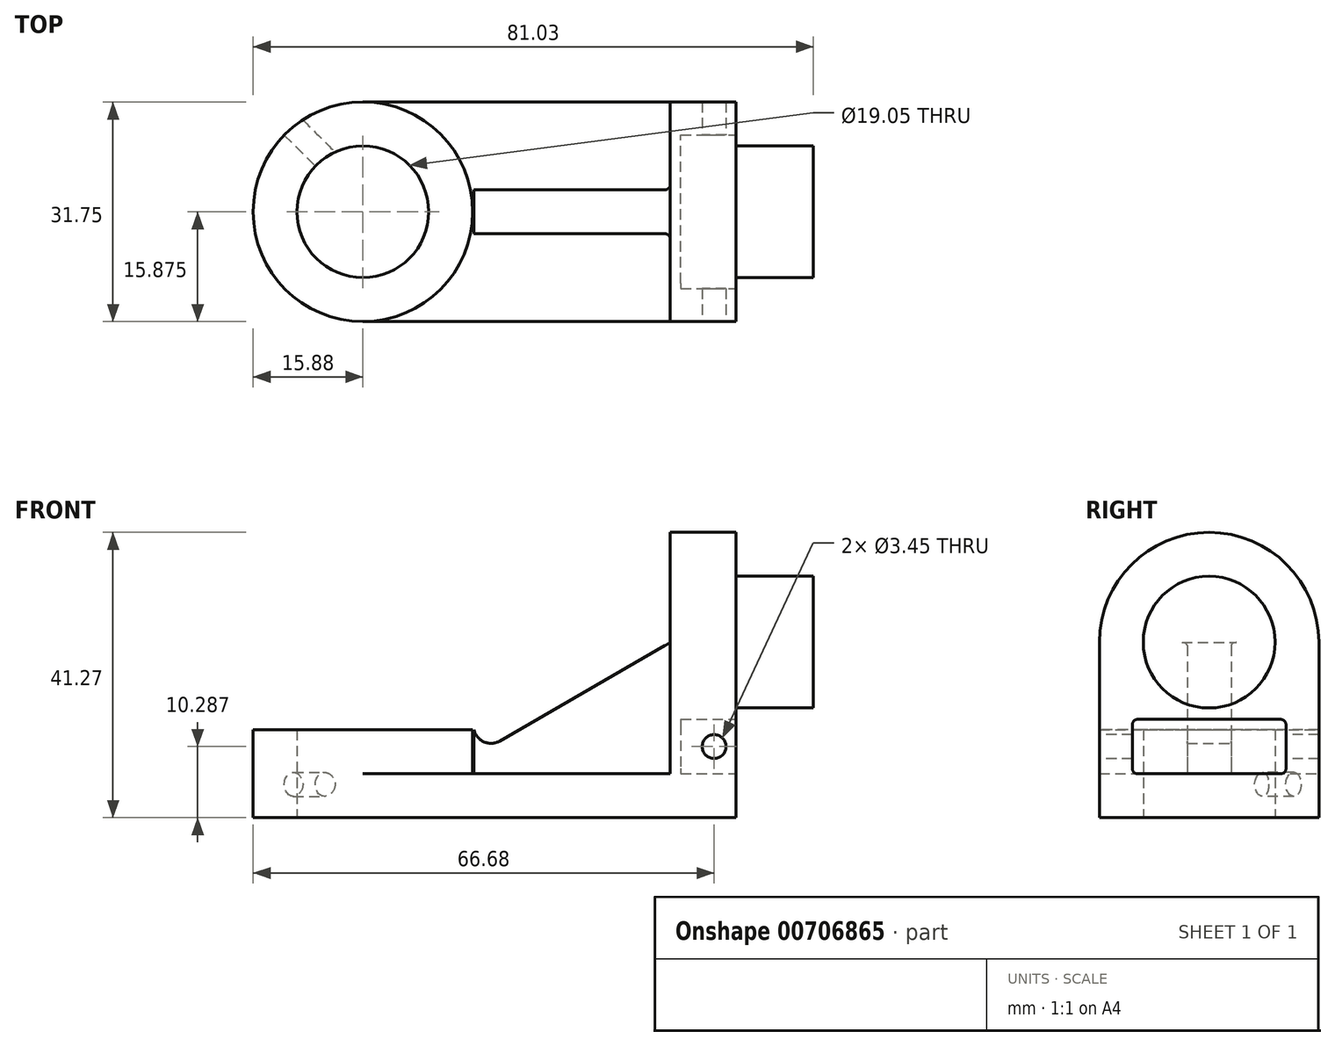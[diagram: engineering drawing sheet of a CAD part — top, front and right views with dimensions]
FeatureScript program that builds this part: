
annotation { "Feature Type Name" : "Feature", "Feature Type Description" : "" }
export const myFeature = defineFeature(function(context is Context, id is Id, definition is map)
    precondition{}
    {
        {
            var Q0;
            Q0=qCreatedBy(makeId("Front.planeOp"),FACE);
            var sketch = newSketch(context, id + "F0", { "sketchPlane" : qUnion([Q0])});
            skLineSegment(sketch, "E0", {"start": v(0, 0) * mm, "end": v(53.97, 0) * mm});
            skLineSegment(sketch, "E1", {"start": v(53.97, 0) * mm, "end": v(53.97, 6.35) * mm});
            skLineSegment(sketch, "E2", {"start": v(53.98, 6.35) * mm, "end": v(0, 6.35) * mm});
            skLineSegment(sketch, "E3", {"start": v(0, 6.35) * mm, "end": v(0, 0) * mm});
            skSolve(sketch);
        }
        {
            var Q0;
            Q0 = qSketchRegion(id + "F0", true);
            extrude(context, id + "F1", {"entities" : qUnion([Q0]), "oppositeDirection" : true, "depth" : 31.75 * mm, "offsetDistance" : 25.4 * mm});
        }
        {
            var Q0;
            Q0=makeQuery(id+"F1.opExtrude","SWEPT_FACE",FACE,{"disambiguationData":[OSD([sQuery(id+"F0.wireOp",EDGE,"E1")])]});
            var sketch = newSketch(context, id + "F2", { "sketchPlane" : qUnion([Q0])});
            skLineSegment(sketch, "E4", {"start": v(0, 0) * mm, "end": v(0, 25.4) * mm});
            skLineSegment(sketch, "E5", {"start": v(0, 0) * mm, "end": v(31.75, 0) * mm});
            skLineSegment(sketch, "E6", {"start": v(31.75, 0) * mm, "end": v(31.75, 25.4) * mm});
            skArc(sketch, "E7", {"start": v(31.75, 25.4) * mm, "mid": v(15.88, 41.28) * mm, "end": v(0, 25.4) * mm});
            skSolve(sketch);
        }
        {
            var Q0;
            Q0 = qSketchRegion(id + "F2", true);
            extrude(context, id + "F3", {"entities" : qUnion([Q0]), "operationType" : NewBodyOperationType.ADD, "oppositeDirection" : true, "depth" : 9.52 * mm, "offsetDistance" : 25.4 * mm});
        }
        {
            var Q0;
            Q0=makeQuery(id+"F3.boolean.opBoolean","MERGE",FACE,{"derivedFrom":[makeQuery(id+"F1.opExtrude","SWEPT_FACE",FACE,{"disambiguationData":[OSD([sQuery(id+"F0.wireOp",EDGE,"E1")])]}),makeQuery(id+"F3.opExtrude","CAP_FACE",FACE,{"disambiguationData":[OSD([sQuery(id+"F2.wireOp",EDGE,"E4"),sQuery(id+"F2.wireOp",EDGE,"E5"),sQuery(id+"F2.wireOp",EDGE,"E6"),sQuery(id+"F2.wireOp",EDGE,"E7")])],"isStart":true})]});
            var sketch = newSketch(context, id + "F4", { "sketchPlane" : qUnion([Q0])});
            skCircle(sketch, "E8", {"center": v(15.88, 25.4) * mm, "radius": 9.53 * mm});
            skSolve(sketch);
        }
        {
            var Q0;
            Q0 = qSketchRegion(id + "F4", true);
            extrude(context, id + "F5", {"entities" : qUnion([Q0]), "operationType" : NewBodyOperationType.ADD, "depth" : 11.18 * mm, "offsetDistance" : 25.4 * mm});
        }
        {
            var Q0;
            Q0=makeQuery(id+"F1.opExtrude","SWEPT_FACE",FACE,{"disambiguationData":[OSD([sQuery(id+"F0.wireOp",EDGE,"E0")])]});
            var sketch = newSketch(context, id + "F6", { "sketchPlane" : qUnion([Q0])});
            skCircle(sketch, "E9", {"center": v(0, -15.88) * mm, "radius": 15.88 * mm});
            skCircle(sketch, "E10", {"center": v(0, -15.88) * mm, "radius": 9.53 * mm});
            skSolve(sketch);
        }
        {
            var Q0;
            Q0 = qSketchRegion(id + "F6", true);
            extrude(context, id + "F7", {"entities" : qUnion([Q0]), "operationType" : NewBodyOperationType.ADD, "oppositeDirection" : true, "depth" : 12.7 * mm, "offsetDistance" : 25.4 * mm});
        }
        {
            var Q0;
            Q0=makeQuery(id+"F7.boolean.opBoolean","SPLIT",FACE,{"disambiguationData":[TD([makeQuery(id+"F1.opExtrude","SWEPT_FACE",FACE,{"disambiguationData":[OSD([sQuery(id+"F0.wireOp",EDGE,"E3")])]})])],"derivedFrom":makeQuery(id+"F1.opExtrude","SWEPT_FACE",FACE,{"disambiguationData":[OSD([sQuery(id+"F0.wireOp",EDGE,"E2")])]})});
            extrude(context, id + "F8", {"entities" : qUnion([Q0]), "operationType" : NewBodyOperationType.REMOVE, "oppositeDirection" : true, "depth" : 25.4 * mm, "offsetDistance" : 25.4 * mm});
        }
        {
            var Q0;
            Q0=makeQuery(id+"F3.boolean.opBoolean","MERGE",FACE,{"derivedFrom":[makeQuery(id+"F1.opExtrude","SWEPT_FACE",FACE,{"disambiguationData":[OSD([sQuery(id+"F0.wireOp",EDGE,"E1")])]}),makeQuery(id+"F3.opExtrude","CAP_FACE",FACE,{"disambiguationData":[OSD([sQuery(id+"F2.wireOp",EDGE,"E4"),sQuery(id+"F2.wireOp",EDGE,"E5"),sQuery(id+"F2.wireOp",EDGE,"E6"),sQuery(id+"F2.wireOp",EDGE,"E7")])],"isStart":true})]});
            var sketch = newSketch(context, id + "F9", { "sketchPlane" : qUnion([Q0])});
            skLineSegment(sketch, "E11.bottom", {"start": v(4.78, 14.22) * mm, "end": v(27, 14.22) * mm});
            skLineSegment(sketch, "E11.top", {"start": v(4.78, 6.35) * mm, "end": v(27, 6.35) * mm});
            skLineSegment(sketch, "E11.left", {"start": v(4.78, 14.22) * mm, "end": v(4.78, 6.35) * mm});
            skLineSegment(sketch, "E11.right", {"start": v(27, 14.22) * mm, "end": v(27, 6.35) * mm});
            skSolve(sketch);
        }
        {
            var Q0;
            Q0 = qSketchRegion(id + "F9", true);
            extrude(context, id + "F10", {"entities" : qUnion([Q0]), "operationType" : NewBodyOperationType.REMOVE, "oppositeDirection" : true, "depth" : 8 * mm, "offsetDistance" : 25.4 * mm});
        }
        {
            var Q0;
            Q0=makeQuery(id+"F3.boolean.opBoolean","MERGE",FACE,{"derivedFrom":[makeQuery(id+"F1.opExtrude","CAP_FACE",FACE,{"disambiguationData":[OSD([sQuery(id+"F0.wireOp",EDGE,"E0"),sQuery(id+"F0.wireOp",EDGE,"E1"),sQuery(id+"F0.wireOp",EDGE,"E2"),sQuery(id+"F0.wireOp",EDGE,"E3")])],"isStart":true}),makeQuery(id+"F3.opExtrude","SWEPT_FACE",FACE,{"disambiguationData":[OSD([sQuery(id+"F2.wireOp",EDGE,"E4")])]})]});
            var sketch = newSketch(context, id + "F11", { "sketchPlane" : qUnion([Q0])});
            skCircle(sketch, "E12", {"center": v(50.8, 10.29) * mm, "radius": 1.73 * mm});
            skSolve(sketch);
        }
        {
            var Q0;
            Q0 = qSketchRegion(id + "F11", true);
            extrude(context, id + "F12", {"entities" : qUnion([Q0]), "operationType" : NewBodyOperationType.REMOVE, "oppositeDirection" : true, "depth" : 31.75 * mm, "offsetDistance" : 25.4 * mm});
        }
        {
            var Q0;
            Q0=makeQuery(id+"F10.boolean.opBoolean","COPY",EDGE,{"derivedFrom":makeQuery(id+"F10.opExtrude","SWEPT_EDGE",EDGE,{"disambiguationData":[OSD([sQuery(id+"F9.wireOp",EDGE,"E11.top"),sQuery(id+"F9.wireOp",EDGE,"E11.right")])]})});
            var Q1;
            Q1=makeQuery(id+"F10.boolean.opBoolean","COPY",EDGE,{"derivedFrom":makeQuery(id+"F10.opExtrude","SWEPT_EDGE",EDGE,{"disambiguationData":[OSD([sQuery(id+"F9.wireOp",EDGE,"E11.bottom"),sQuery(id+"F9.wireOp",EDGE,"E11.right")])]})});
            var Q2;
            Q2=makeQuery(id+"F10.boolean.opBoolean","COPY",EDGE,{"derivedFrom":makeQuery(id+"F10.opExtrude","SWEPT_EDGE",EDGE,{"disambiguationData":[OSD([sQuery(id+"F9.wireOp",EDGE,"E11.top"),sQuery(id+"F9.wireOp",EDGE,"E11.left")])]})});
            var Q3;
            Q3=makeQuery(id+"F10.boolean.opBoolean","COPY",EDGE,{"derivedFrom":makeQuery(id+"F10.opExtrude","SWEPT_EDGE",EDGE,{"disambiguationData":[OSD([sQuery(id+"F9.wireOp",EDGE,"E11.bottom"),sQuery(id+"F9.wireOp",EDGE,"E11.left")])]})});
            fillet(context, id + "F13", {"entities" : qUnion([Q0, Q1, Q2, Q3]), "radius" : 0.76 * mm, "tangentPropagation" : true, "allowEdgeOverflow" : false});
        }
        {
            var Q0;
            Q0=qCreatedBy(makeId("Front.planeOp"),FACE);
            cPlane(context, id + "F14", {"entities" : qUnion([Q0]), "cplaneType" : CPlaneType.OFFSET, "offset" : 15.88 * mm, "oppositeDirection" : true, "width" : 152.4 * mm, "height" : 152.4 * mm});
        }
        {
            var Q0;
            Q0=qCreatedBy(id+"F14.planeOp",FACE);
            var Q1;
            Q1=qCreatedBy(makeId("Right.planeOp"),FACE);
            cPlane(context, id + "F15", {"entities" : qUnion([Q0, Q1]), "cplaneType" : CPlaneType.MID_PLANE, "offset" : 25.4 * mm, "flipAlignment" : true, "width" : 152.4 * mm, "height" : 152.4 * mm});
        }
        {
            var Q0;
            Q0=qCreatedBy(id+"F14.planeOp",FACE);
            var sketch = newSketch(context, id + "F16", { "sketchPlane" : qUnion([Q0])});
            skLineSegment(sketch, "E13", {"start": v(16.07, 12.7) * mm, "end": v(16.07, 6.35) * mm});
            skLineSegment(sketch, "E14", {"start": v(16.07, 6.35) * mm, "end": v(44.57, 6.35) * mm});
            skLineSegment(sketch, "E15", {"start": v(44.57, 6.35) * mm, "end": v(44.57, 25.4) * mm});
            skLineSegment(sketch, "E16", {"start": v(44.57, 25.4) * mm, "end": v(19.8, 11.1) * mm});
            skArc(sketch, "E17", {"start": v(16.07, 12.7) * mm, "mid": v(17.54, 10.97) * mm, "end": v(19.8, 11.1) * mm});
            skSolve(sketch);
        }
        {
            var Q0;
            Q0 = qSketchRegion(id + "F16", true);
            extrude(context, id + "F17", {"entities" : qUnion([Q0]), "operationType" : NewBodyOperationType.ADD, "endBound" : BoundingType.SYMMETRIC, "depth" : 6.35 * mm, "offsetDistance" : 25.4 * mm});
        }
        {
            var Q0;
            Q0=makeQuery(id+"F17.boolean.opBoolean","INTERSECT",EDGE,{"derivedFrom":[makeQuery(id+"F3.opExtrude","CAP_FACE",FACE,{"disambiguationData":[OSD([sQuery(id+"F2.wireOp",EDGE,"E4"),sQuery(id+"F2.wireOp",EDGE,"E5"),sQuery(id+"F2.wireOp",EDGE,"E6"),sQuery(id+"F2.wireOp",EDGE,"E7")])],"isStart":false}),makeQuery(id+"F17.opExtrude","CAP_FACE",FACE,{"disambiguationData":[OSD([sQuery(id+"F16.wireOp",EDGE,"E13"),sQuery(id+"F16.wireOp",EDGE,"E14"),sQuery(id+"F16.wireOp",EDGE,"E15"),sQuery(id+"F16.wireOp",EDGE,"E16"),sQuery(id+"F16.wireOp",EDGE,"E17")])],"isStart":false})]});
            var Q1;
            Q1=makeQuery(id+"F17.boolean.opBoolean","INTERSECT",EDGE,{"derivedFrom":[makeQuery(id+"F3.opExtrude","CAP_FACE",FACE,{"disambiguationData":[OSD([sQuery(id+"F2.wireOp",EDGE,"E4"),sQuery(id+"F2.wireOp",EDGE,"E5"),sQuery(id+"F2.wireOp",EDGE,"E6"),sQuery(id+"F2.wireOp",EDGE,"E7")])],"isStart":false}),makeQuery(id+"F17.opExtrude","CAP_FACE",FACE,{"disambiguationData":[OSD([sQuery(id+"F16.wireOp",EDGE,"E13"),sQuery(id+"F16.wireOp",EDGE,"E14"),sQuery(id+"F16.wireOp",EDGE,"E15"),sQuery(id+"F16.wireOp",EDGE,"E16"),sQuery(id+"F16.wireOp",EDGE,"E17")])],"isStart":true})]});
            fillet(context, id + "F18", {"entities" : qUnion([Q0, Q1]), "radius" : 0.76 * mm, "tangentPropagation" : true, "allowEdgeOverflow" : false});
        }
        {
            var Q0;
            Q0=qCreatedBy(id+"F15.planeOp",FACE);
            var sketch = newSketch(context, id + "F19", { "sketchPlane" : qUnion([Q0])});
            skCircle(sketch, "E18", {"center": v(12.76, 4.83) * mm, "radius": 1.73 * mm});
            skSolve(sketch);
        }
        {
            var Q0;
            Q0 = qSketchRegion(id + "F19", true);
            extrude(context, id + "F20", {"entities" : qUnion([Q0]), "operationType" : NewBodyOperationType.REMOVE, "oppositeDirection" : true, "depth" : 25.4 * mm, "offsetDistance" : 25.4 * mm});
        }
    });
